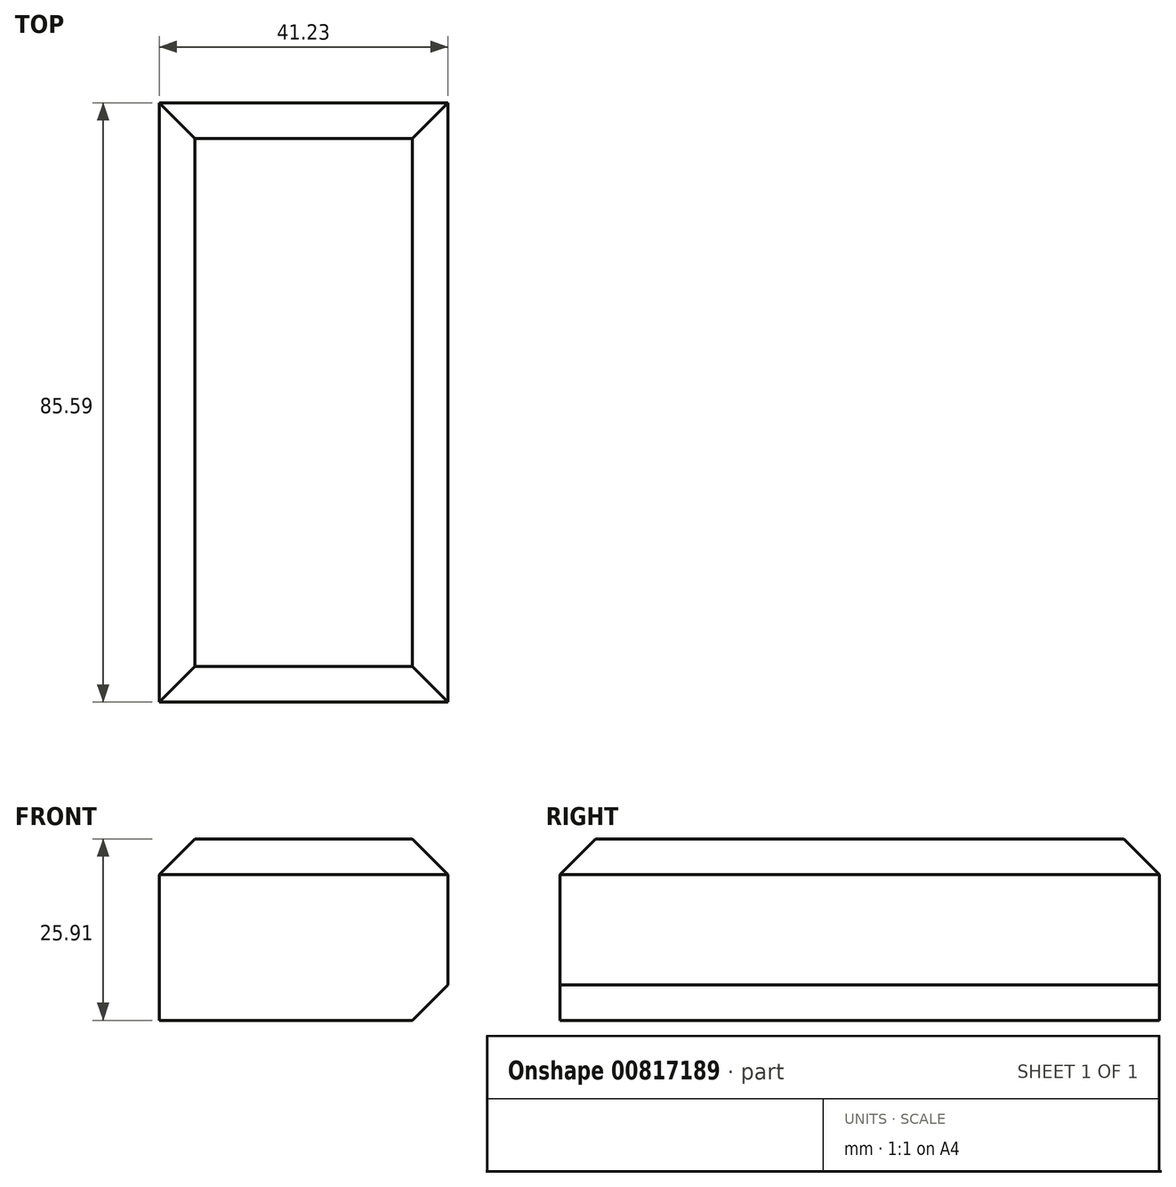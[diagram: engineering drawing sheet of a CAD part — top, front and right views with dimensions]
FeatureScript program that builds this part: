
annotation { "Feature Type Name" : "Feature", "Feature Type Description" : "" }
export const myFeature = defineFeature(function(context is Context, id is Id, definition is map)
    precondition{}
    {
        {
            var Q0;
            Q0=qCreatedBy(makeId("Top.planeOp"),FACE);
            var sketch = newSketch(context, id + "F0", { "sketchPlane" : qUnion([Q0])});
            skLineSegment(sketch, "E0.bottom", {"start": v(-127.44, -43.96) * mm, "end": v(-86.21, -43.96) * mm});
            skLineSegment(sketch, "E0.top", {"start": v(-127.44, 41.63) * mm, "end": v(-86.21, 41.63) * mm});
            skLineSegment(sketch, "E0.left", {"start": v(-127.44, -43.96) * mm, "end": v(-127.44, 41.63) * mm});
            skLineSegment(sketch, "E0.right", {"start": v(-86.21, -43.96) * mm, "end": v(-86.21, 41.63) * mm});
            skSolve(sketch);
        }
        {
            var Q0;
            Q0=makeQuery(id+"F0.imprint","IMPRINT",FACE,{"disambiguationData":[TD([[makeQuery(id+"F0.imprint","IMPRINT",EDGE,{"derivedFrom":sQuery(id+"F0.wireOp",EDGE,"E0.bottom")}),1.0]])]});
            extrude(context, id + "F1", {"entities" : qUnion([Q0]), "depth" : 25.9 * mm, "offsetDistance" : 25.4 * mm});
        }
        {
            var Q0;
            Q0=makeQuery(id+"F1.opExtrude","CAP_FACE",FACE,{"disambiguationData":[OSD([sQuery(id+"F0.wireOp",EDGE,"E0.bottom"),sQuery(id+"F0.wireOp",EDGE,"E0.top"),sQuery(id+"F0.wireOp",EDGE,"E0.left"),sQuery(id+"F0.wireOp",EDGE,"E0.right")])],"isStart":false});
            var Q1;
            Q1=makeQuery(id+"F1.opExtrude","CAP_EDGE",EDGE,{"disambiguationData":[OSD([sQuery(id+"F0.wireOp",EDGE,"E0.right")])],"isStart":true});
            chamfer(context, id + "F2", {"entities" : qUnion([Q0, Q1]), "width" : 5.08 * mm, "tangentPropagation" : true});
        }
    });
